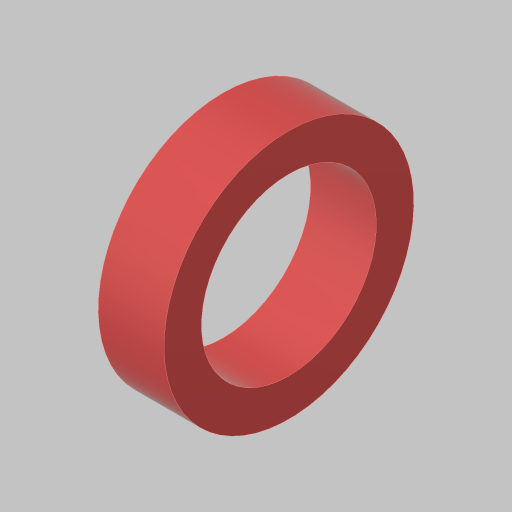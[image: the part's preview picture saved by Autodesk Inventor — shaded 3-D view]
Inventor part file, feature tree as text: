
AUTODESK INVENTOR PART (.ipt)
format: ipt  version: 2023.5 (Build 275446000, 446)  size: 107,008 bytes
history: native  units: in
note: dims shown in document units (in); Inventor stores cm internally (conversion verified against a paired STEP export)
features: extrude x1, sketch x1
ambient origin geometry x8: Origin, YZ Plane, XZ Plane, XY Plane, X Axis, Y Axis, Z Axis, Center Point
bodies: Solid1 (feature_tree)
feature tree (2):
  extrude  "Extrusion1"  Depth=0.22in
  sketch  "Sketch1"  dims[d0=0.585in d1=0.125in d2=0.22in d3=0.0in]
